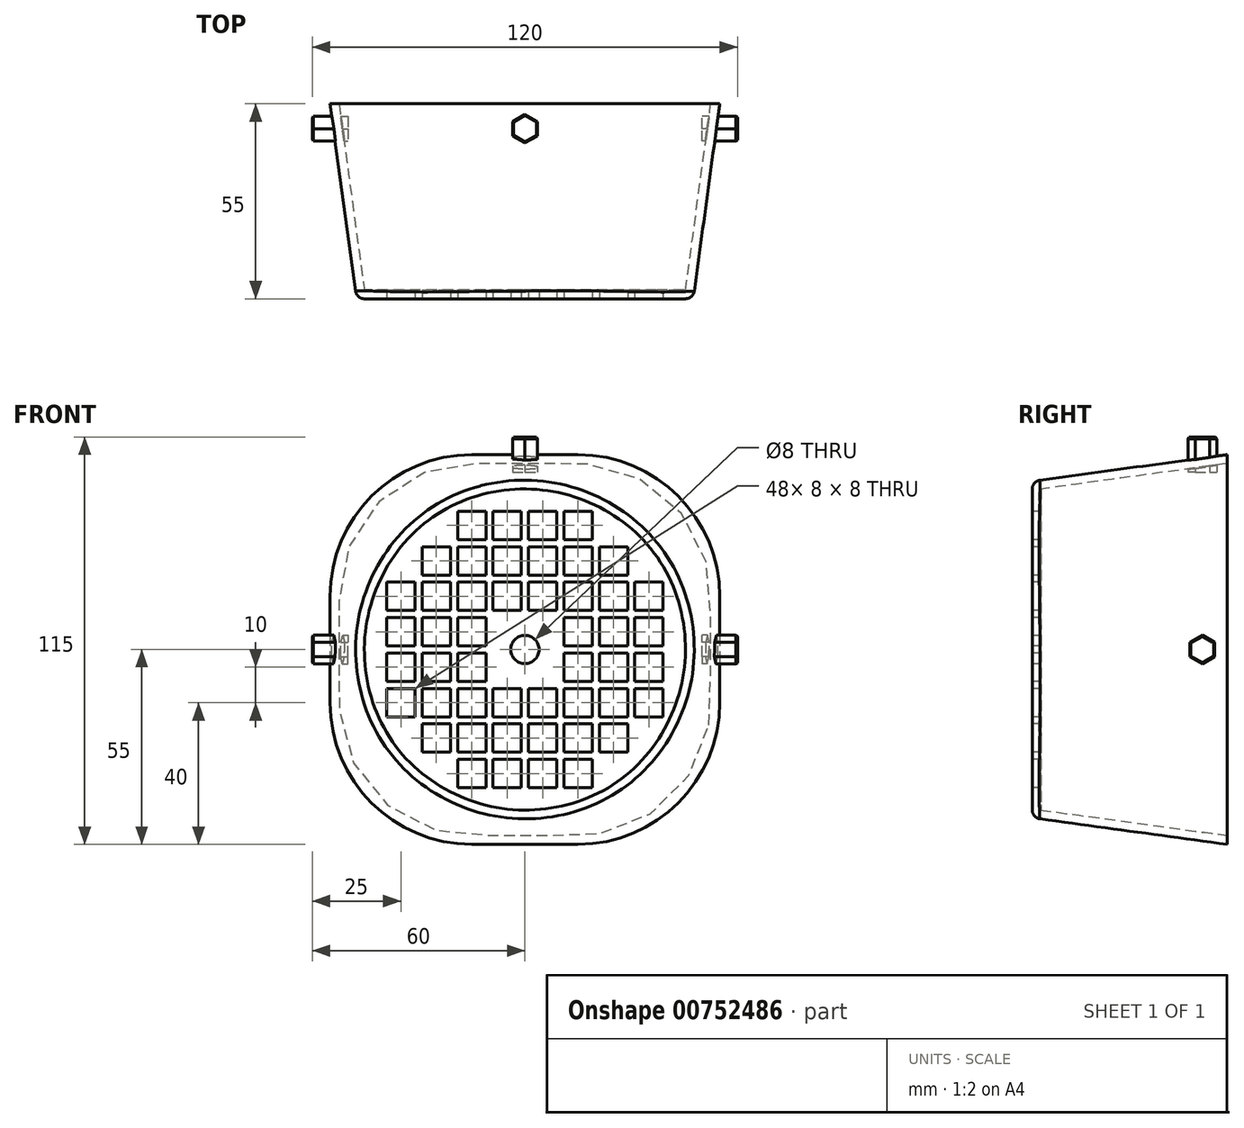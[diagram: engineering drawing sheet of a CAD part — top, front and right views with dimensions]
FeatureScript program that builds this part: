
annotation { "Feature Type Name" : "Feature", "Feature Type Description" : "" }
export const myFeature = defineFeature(function(context is Context, id is Id, definition is map)
    precondition{}
    {
        {
            var Q0;
            Q0=qCreatedBy(makeId("Front.planeOp"),FACE);
            var sketch = newSketch(context, id + "F0", { "sketchPlane" : qUnion([Q0])});
            skLineSegment(sketch, "E0.bottom", {"start": v(-15, 55) * mm, "end": v(15, 55) * mm});
            skLineSegment(sketch, "E0.top", {"start": v(-15, -55) * mm, "end": v(15, -55) * mm});
            skLineSegment(sketch, "E0.left", {"start": v(-55, 15) * mm, "end": v(-55, -15) * mm});
            skLineSegment(sketch, "E0.right", {"start": v(55, 15) * mm, "end": v(55, -15) * mm});
            skPoint(sketch, "E0.middle", {"position": v(0, 0) * mm});
            skPoint(sketch, "E1.visualSharp", {"position": v(-55, 55) * mm});
            skArc(sketch, "E1.filletArc", {"start": v(-15, 55) * mm, "mid": v(-43.28, 43.28) * mm, "end": v(-55, 15) * mm});
            skPoint(sketch, "E2.visualSharp", {"position": v(55, 55) * mm});
            skArc(sketch, "E2.filletArc", {"start": v(55, 15) * mm, "mid": v(43.28, 43.28) * mm, "end": v(15, 55) * mm});
            skPoint(sketch, "E3.visualSharp", {"position": v(55, -55) * mm});
            skArc(sketch, "E3.filletArc", {"start": v(15, -55) * mm, "mid": v(43.28, -43.28) * mm, "end": v(55, -15) * mm});
            skPoint(sketch, "E4.visualSharp", {"position": v(-55, -55) * mm});
            skArc(sketch, "E4.filletArc", {"start": v(-55, -15) * mm, "mid": v(-43.28, -43.28) * mm, "end": v(-15, -55) * mm});
            skSolve(sketch);
        }
        {
            var Q0;
            Q0=qCreatedBy(makeId("Front.planeOp"),FACE);
            cPlane(context, id + "F1", {"entities" : qUnion([Q0]), "cplaneType" : CPlaneType.OFFSET, "offset" : 55 * mm, "width" : 150 * mm, "height" : 150 * mm});
        }
        {
            var Q0;
            Q0=qCreatedBy(id+"F1.planeOp",FACE);
            var sketch = newSketch(context, id + "F2", { "sketchPlane" : qUnion([Q0])});
            skCircle(sketch, "E5", {"center": v(0, 0) * mm, "radius": 47.5 * mm});
            skSolve(sketch);
        }
        {
            var Q0;
            Q0=makeQuery(id+"F0.imprint","IMPRINT",FACE,{"disambiguationData":[TD([[makeQuery(id+"F0.imprint","IMPRINT",EDGE,{"derivedFrom":sQuery(id+"F0.wireOp",EDGE,"E0.bottom")}),-1.0]])]});
            var Q1;
            Q1=makeQuery(id+"F2.imprint","IMPRINT",FACE,{"disambiguationData":[TD([[makeQuery(id+"F2.imprint","IMPRINT",EDGE,{"derivedFrom":sQuery(id+"F2.wireOp",EDGE,"E5")}),1.0]])]});
            loft(context, id + "F3", {"sheetProfilesArray" : [{ "sheetProfileEntities" : qUnion([Q0]) }, { "sheetProfileEntities" : qUnion([Q1]) }]});
        }
        {
            var Q0;
            Q0=makeQuery(id+"F3.opLoft","CAP_FACE",FACE,{"disambiguationData":[OSD([makeQuery(id+"F2.imprint","IMPRINT",FACE,{"disambiguationData":[TD([[makeQuery(id+"F2.imprint","IMPRINT",EDGE,{"derivedFrom":sQuery(id+"F2.wireOp",EDGE,"E5")}),1.0]])]})])],"isStart":true});
            fillet(context, id + "F4", {"entities" : qUnion([Q0]), "radius" : 2.5 * mm, "tangentPropagation" : true, "allowEdgeOverflow" : false});
        }
        {
            var Q0;
            Q0=makeQuery(id+"F3.opLoft","CAP_FACE",FACE,{"disambiguationData":[OSD([makeQuery(id+"F0.imprint","IMPRINT",FACE,{"disambiguationData":[TD([[makeQuery(id+"F0.imprint","IMPRINT",EDGE,{"derivedFrom":sQuery(id+"F0.wireOp",EDGE,"E0.bottom")}),-1.0]])]})])],"isStart":true});
            shell(context, id + "F5", {"entities" : qUnion([Q0]), "thickness" : 2.5 * mm});
        }
        {
            var Q0;
            Q0=makeQuery(id+"F3.opLoft","CAP_FACE",FACE,{"disambiguationData":[OSD([makeQuery(id+"F2.imprint","IMPRINT",FACE,{"disambiguationData":[TD([[makeQuery(id+"F2.imprint","IMPRINT",EDGE,{"derivedFrom":sQuery(id+"F2.wireOp",EDGE,"E5")}),1.0]])]})])],"isStart":true});
            var sketch = newSketch(context, id + "F6", { "sketchPlane" : qUnion([Q0])});
            skLineSegment(sketch, "E6.bottom", {"start": v(11, 11) * mm, "end": v(-11, 11) * mm, "construction": true});
            skLineSegment(sketch, "E6.top", {"start": v(11, -11) * mm, "end": v(-11, -11) * mm, "construction": true});
            skLineSegment(sketch, "E6.left", {"start": v(11, 11) * mm, "end": v(11, -11) * mm, "construction": true});
            skLineSegment(sketch, "E6.right", {"start": v(-11, 11) * mm, "end": v(-11, -11) * mm, "construction": true});
            skPoint(sketch, "E6.middle", {"position": v(0, 0) * mm});
            skLineSegment(sketch, "E7.bottom", {"start": v(-11, 9) * mm, "end": v(-19, 9) * mm});
            skLineSegment(sketch, "E7.top", {"start": v(-11, 1) * mm, "end": v(-19, 1) * mm});
            skLineSegment(sketch, "E7.left", {"start": v(-11, 9) * mm, "end": v(-11, 1) * mm});
            skLineSegment(sketch, "E7.right", {"start": v(-19, 9) * mm, "end": v(-19, 1) * mm});
            skPoint(sketch, "E7.middle", {"position": v(-15, 5) * mm});
            skLineSegment(sketch, "E8.0.1.0", {"start": v(-11, -1) * mm, "end": v(-19, -1) * mm});
            skLineSegment(sketch, "E8.0.1.1", {"start": v(-19, -1) * mm, "end": v(-19, -9) * mm});
            skLineSegment(sketch, "E8.0.1.2", {"start": v(-11, -1) * mm, "end": v(-11, -9) * mm});
            skPoint(sketch, "E8.0.1.3", {"position": v(-15, -5) * mm});
            skLineSegment(sketch, "E8.0.1.4", {"start": v(-11, -9) * mm, "end": v(-19, -9) * mm});
            skLineSegment(sketch, "E8.0.2.0", {"start": v(-11, -11) * mm, "end": v(-19, -11) * mm});
            skLineSegment(sketch, "E8.0.2.1", {"start": v(-19, -11) * mm, "end": v(-19, -19) * mm});
            skLineSegment(sketch, "E8.0.2.2", {"start": v(-11, -11) * mm, "end": v(-11, -19) * mm});
            skPoint(sketch, "E8.0.2.3", {"position": v(-15, -15) * mm});
            skLineSegment(sketch, "E8.0.2.4", {"start": v(-11, -19) * mm, "end": v(-19, -19) * mm});
            skLineSegment(sketch, "E8.0.3.0", {"start": v(-11, -21) * mm, "end": v(-19, -21) * mm});
            skLineSegment(sketch, "E8.0.3.1", {"start": v(-19, -21) * mm, "end": v(-19, -29) * mm});
            skLineSegment(sketch, "E8.0.3.2", {"start": v(-11, -21) * mm, "end": v(-11, -29) * mm});
            skPoint(sketch, "E8.0.3.3", {"position": v(-15, -25) * mm});
            skLineSegment(sketch, "E8.0.3.4", {"start": v(-11, -29) * mm, "end": v(-19, -29) * mm});
            skLineSegment(sketch, "E8.0.4.0", {"start": v(-11, -31) * mm, "end": v(-19, -31) * mm});
            skLineSegment(sketch, "E8.0.4.1", {"start": v(-19, -31) * mm, "end": v(-19, -39) * mm});
            skLineSegment(sketch, "E8.0.4.2", {"start": v(-11, -31) * mm, "end": v(-11, -39) * mm});
            skPoint(sketch, "E8.0.4.3", {"position": v(-15, -35) * mm});
            skLineSegment(sketch, "E8.0.4.4", {"start": v(-11, -39) * mm, "end": v(-19, -39) * mm});
            skLineSegment(sketch, "E8.1.0.0", {"start": v(-21, 9) * mm, "end": v(-29, 9) * mm});
            skLineSegment(sketch, "E8.1.0.1", {"start": v(-29, 9) * mm, "end": v(-29, 1) * mm});
            skLineSegment(sketch, "E8.1.0.2", {"start": v(-21, 9) * mm, "end": v(-21, 1) * mm});
            skPoint(sketch, "E8.1.0.3", {"position": v(-25, 5) * mm});
            skLineSegment(sketch, "E8.1.0.4", {"start": v(-21, 1) * mm, "end": v(-29, 1) * mm});
            skLineSegment(sketch, "E8.1.1.0", {"start": v(-21, -1) * mm, "end": v(-29, -1) * mm});
            skLineSegment(sketch, "E8.1.1.1", {"start": v(-29, -1) * mm, "end": v(-29, -9) * mm});
            skLineSegment(sketch, "E8.1.1.2", {"start": v(-21, -1) * mm, "end": v(-21, -9) * mm});
            skPoint(sketch, "E8.1.1.3", {"position": v(-25, -5) * mm});
            skLineSegment(sketch, "E8.1.1.4", {"start": v(-21, -9) * mm, "end": v(-29, -9) * mm});
            skLineSegment(sketch, "E8.1.2.0", {"start": v(-21, -11) * mm, "end": v(-29, -11) * mm});
            skLineSegment(sketch, "E8.1.2.1", {"start": v(-29, -11) * mm, "end": v(-29, -19) * mm});
            skLineSegment(sketch, "E8.1.2.2", {"start": v(-21, -11) * mm, "end": v(-21, -19) * mm});
            skPoint(sketch, "E8.1.2.3", {"position": v(-25, -15) * mm});
            skLineSegment(sketch, "E8.1.2.4", {"start": v(-21, -19) * mm, "end": v(-29, -19) * mm});
            skLineSegment(sketch, "E8.1.3.0", {"start": v(-21, -21) * mm, "end": v(-29, -21) * mm});
            skLineSegment(sketch, "E8.1.3.1", {"start": v(-29, -21) * mm, "end": v(-29, -29) * mm});
            skLineSegment(sketch, "E8.1.3.2", {"start": v(-21, -21) * mm, "end": v(-21, -29) * mm});
            skPoint(sketch, "E8.1.3.3", {"position": v(-25, -25) * mm});
            skLineSegment(sketch, "E8.1.3.4", {"start": v(-21, -29) * mm, "end": v(-29, -29) * mm});
            skLineSegment(sketch, "E8.2.0.0", {"start": v(-31, 9) * mm, "end": v(-39, 9) * mm});
            skLineSegment(sketch, "E8.2.0.1", {"start": v(-39, 9) * mm, "end": v(-39, 1) * mm});
            skLineSegment(sketch, "E8.2.0.2", {"start": v(-31, 9) * mm, "end": v(-31, 1) * mm});
            skPoint(sketch, "E8.2.0.3", {"position": v(-35, 5) * mm});
            skLineSegment(sketch, "E8.2.0.4", {"start": v(-31, 1) * mm, "end": v(-39, 1) * mm});
            skLineSegment(sketch, "E8.2.1.0", {"start": v(-31, -1) * mm, "end": v(-39, -1) * mm});
            skLineSegment(sketch, "E8.2.1.1", {"start": v(-39, -1) * mm, "end": v(-39, -9) * mm});
            skLineSegment(sketch, "E8.2.1.2", {"start": v(-31, -1) * mm, "end": v(-31, -9) * mm});
            skPoint(sketch, "E8.2.1.3", {"position": v(-35, -5) * mm});
            skLineSegment(sketch, "E8.2.1.4", {"start": v(-31, -9) * mm, "end": v(-39, -9) * mm});
            skLineSegment(sketch, "E8.2.2.0", {"start": v(-31, -11) * mm, "end": v(-39, -11) * mm});
            skLineSegment(sketch, "E8.2.2.1", {"start": v(-39, -11) * mm, "end": v(-39, -19) * mm});
            skLineSegment(sketch, "E8.2.2.2", {"start": v(-31, -11) * mm, "end": v(-31, -19) * mm});
            skPoint(sketch, "E8.2.2.3", {"position": v(-35, -15) * mm});
            skLineSegment(sketch, "E8.2.2.4", {"start": v(-31, -19) * mm, "end": v(-39, -19) * mm});
            skLineSegment(sketch, "E8.direction1", {"start": v(-19, 9) * mm, "end": v(-29, 9) * mm, "construction": true});
            skLineSegment(sketch, "E8.direction2", {"start": v(-19, 9) * mm, "end": v(-19, -1) * mm, "construction": true});
            skLineSegment(sketch, "E9.0.1.0", {"start": v(-11, 19) * mm, "end": v(-19, 19) * mm});
            skLineSegment(sketch, "E9.0.1.1", {"start": v(-11, 19) * mm, "end": v(-11, 11) * mm});
            skLineSegment(sketch, "E9.0.1.2", {"start": v(-19, 19) * mm, "end": v(-19, 11) * mm});
            skLineSegment(sketch, "E9.0.1.3", {"start": v(-11, 11) * mm, "end": v(-19, 11) * mm});
            skLineSegment(sketch, "E9.0.2.0", {"start": v(-11, 29) * mm, "end": v(-19, 29) * mm});
            skLineSegment(sketch, "E9.0.2.1", {"start": v(-11, 29) * mm, "end": v(-11, 21) * mm});
            skLineSegment(sketch, "E9.0.2.2", {"start": v(-19, 29) * mm, "end": v(-19, 21) * mm});
            skLineSegment(sketch, "E9.0.2.3", {"start": v(-11, 21) * mm, "end": v(-19, 21) * mm});
            skLineSegment(sketch, "E9.0.3.0", {"start": v(-11, 39) * mm, "end": v(-19, 39) * mm});
            skLineSegment(sketch, "E9.0.3.1", {"start": v(-11, 39) * mm, "end": v(-11, 31) * mm});
            skLineSegment(sketch, "E9.0.3.2", {"start": v(-19, 39) * mm, "end": v(-19, 31) * mm});
            skLineSegment(sketch, "E9.0.3.3", {"start": v(-11, 31) * mm, "end": v(-19, 31) * mm});
            skLineSegment(sketch, "E9.1.1.0", {"start": v(-1, 19) * mm, "end": v(-9, 19) * mm});
            skLineSegment(sketch, "E9.1.1.1", {"start": v(-1, 19) * mm, "end": v(-1, 11) * mm});
            skLineSegment(sketch, "E9.1.1.2", {"start": v(-9, 19) * mm, "end": v(-9, 11) * mm});
            skLineSegment(sketch, "E9.1.1.3", {"start": v(-1, 11) * mm, "end": v(-9, 11) * mm});
            skLineSegment(sketch, "E9.1.2.0", {"start": v(-1, 29) * mm, "end": v(-9, 29) * mm});
            skLineSegment(sketch, "E9.1.2.1", {"start": v(-1, 29) * mm, "end": v(-1, 21) * mm});
            skLineSegment(sketch, "E9.1.2.2", {"start": v(-9, 29) * mm, "end": v(-9, 21) * mm});
            skLineSegment(sketch, "E9.1.2.3", {"start": v(-1, 21) * mm, "end": v(-9, 21) * mm});
            skLineSegment(sketch, "E9.1.3.0", {"start": v(-1, 39) * mm, "end": v(-9, 39) * mm});
            skLineSegment(sketch, "E9.1.3.1", {"start": v(-1, 39) * mm, "end": v(-1, 31) * mm});
            skLineSegment(sketch, "E9.1.3.2", {"start": v(-9, 39) * mm, "end": v(-9, 31) * mm});
            skLineSegment(sketch, "E9.1.3.3", {"start": v(-1, 31) * mm, "end": v(-9, 31) * mm});
            skLineSegment(sketch, "E9.2.1.0", {"start": v(9, 19) * mm, "end": v(1, 19) * mm});
            skLineSegment(sketch, "E9.2.1.1", {"start": v(9, 19) * mm, "end": v(9, 11) * mm});
            skLineSegment(sketch, "E9.2.1.2", {"start": v(1, 19) * mm, "end": v(1, 11) * mm});
            skLineSegment(sketch, "E9.2.1.3", {"start": v(9, 11) * mm, "end": v(1, 11) * mm});
            skLineSegment(sketch, "E9.2.2.0", {"start": v(9, 29) * mm, "end": v(1, 29) * mm});
            skLineSegment(sketch, "E9.2.2.1", {"start": v(9, 29) * mm, "end": v(9, 21) * mm});
            skLineSegment(sketch, "E9.2.2.2", {"start": v(1, 29) * mm, "end": v(1, 21) * mm});
            skLineSegment(sketch, "E9.2.2.3", {"start": v(9, 21) * mm, "end": v(1, 21) * mm});
            skLineSegment(sketch, "E9.2.3.0", {"start": v(9, 39) * mm, "end": v(1, 39) * mm});
            skLineSegment(sketch, "E9.2.3.1", {"start": v(9, 39) * mm, "end": v(9, 31) * mm});
            skLineSegment(sketch, "E9.2.3.2", {"start": v(1, 39) * mm, "end": v(1, 31) * mm});
            skLineSegment(sketch, "E9.2.3.3", {"start": v(9, 31) * mm, "end": v(1, 31) * mm});
            skLineSegment(sketch, "E9.3.0.0", {"start": v(19, 9) * mm, "end": v(11, 9) * mm});
            skLineSegment(sketch, "E9.3.0.1", {"start": v(19, 9) * mm, "end": v(19, 1) * mm});
            skLineSegment(sketch, "E9.3.0.2", {"start": v(11, 9) * mm, "end": v(11, 1) * mm});
            skLineSegment(sketch, "E9.3.0.3", {"start": v(19, 1) * mm, "end": v(11, 1) * mm});
            skLineSegment(sketch, "E9.3.1.0", {"start": v(19, 19) * mm, "end": v(11, 19) * mm});
            skLineSegment(sketch, "E9.3.1.1", {"start": v(19, 19) * mm, "end": v(19, 11) * mm});
            skLineSegment(sketch, "E9.3.1.2", {"start": v(11, 19) * mm, "end": v(11, 11) * mm});
            skLineSegment(sketch, "E9.3.1.3", {"start": v(19, 11) * mm, "end": v(11, 11) * mm});
            skLineSegment(sketch, "E9.3.2.0", {"start": v(19, 29) * mm, "end": v(11, 29) * mm});
            skLineSegment(sketch, "E9.3.2.1", {"start": v(19, 29) * mm, "end": v(19, 21) * mm});
            skLineSegment(sketch, "E9.3.2.2", {"start": v(11, 29) * mm, "end": v(11, 21) * mm});
            skLineSegment(sketch, "E9.3.2.3", {"start": v(19, 21) * mm, "end": v(11, 21) * mm});
            skLineSegment(sketch, "E9.3.3.0", {"start": v(19, 39) * mm, "end": v(11, 39) * mm});
            skLineSegment(sketch, "E9.3.3.1", {"start": v(19, 39) * mm, "end": v(19, 31) * mm});
            skLineSegment(sketch, "E9.3.3.2", {"start": v(11, 39) * mm, "end": v(11, 31) * mm});
            skLineSegment(sketch, "E9.3.3.3", {"start": v(19, 31) * mm, "end": v(11, 31) * mm});
            skLineSegment(sketch, "E9.4.0.0", {"start": v(29, 9) * mm, "end": v(21, 9) * mm});
            skLineSegment(sketch, "E9.4.0.1", {"start": v(29, 9) * mm, "end": v(29, 1) * mm});
            skLineSegment(sketch, "E9.4.0.2", {"start": v(21, 9) * mm, "end": v(21, 1) * mm});
            skLineSegment(sketch, "E9.4.0.3", {"start": v(29, 1) * mm, "end": v(21, 1) * mm});
            skLineSegment(sketch, "E9.4.1.0", {"start": v(29, 19) * mm, "end": v(21, 19) * mm});
            skLineSegment(sketch, "E9.4.1.1", {"start": v(29, 19) * mm, "end": v(29, 11) * mm});
            skLineSegment(sketch, "E9.4.1.2", {"start": v(21, 19) * mm, "end": v(21, 11) * mm});
            skLineSegment(sketch, "E9.4.1.3", {"start": v(29, 11) * mm, "end": v(21, 11) * mm});
            skLineSegment(sketch, "E9.4.2.0", {"start": v(29, 29) * mm, "end": v(21, 29) * mm});
            skLineSegment(sketch, "E9.4.2.1", {"start": v(29, 29) * mm, "end": v(29, 21) * mm});
            skLineSegment(sketch, "E9.4.2.2", {"start": v(21, 29) * mm, "end": v(21, 21) * mm});
            skLineSegment(sketch, "E9.4.2.3", {"start": v(29, 21) * mm, "end": v(21, 21) * mm});
            skLineSegment(sketch, "E9.direction1", {"start": v(-19, 1) * mm, "end": v(-9, 1) * mm, "construction": true});
            skLineSegment(sketch, "E9.direction2", {"start": v(-19, 1) * mm, "end": v(-19, 11) * mm, "construction": true});
            skLineSegment(sketch, "E10.1.0.4", {"start": v(-21, 29) * mm, "end": v(-29, 29) * mm});
            skLineSegment(sketch, "E10.1.0.5", {"start": v(-21, 29) * mm, "end": v(-21, 21) * mm});
            skLineSegment(sketch, "E10.1.0.6", {"start": v(-21, 21) * mm, "end": v(-29, 21) * mm});
            skLineSegment(sketch, "E10.1.0.7", {"start": v(-21, 19) * mm, "end": v(-29, 19) * mm});
            skLineSegment(sketch, "E10.1.0.8", {"start": v(-21, 19) * mm, "end": v(-21, 11) * mm});
            skLineSegment(sketch, "E10.1.0.9", {"start": v(-21, 11) * mm, "end": v(-29, 11) * mm});
            skLineSegment(sketch, "E10.1.0.10", {"start": v(-29, 19) * mm, "end": v(-29, 11) * mm});
            skLineSegment(sketch, "E10.1.0.11", {"start": v(-29, 29) * mm, "end": v(-29, 21) * mm});
            skLineSegment(sketch, "E10.2.0.7", {"start": v(-31, 19) * mm, "end": v(-39, 19) * mm});
            skLineSegment(sketch, "E10.2.0.8", {"start": v(-31, 19) * mm, "end": v(-31, 11) * mm});
            skLineSegment(sketch, "E10.2.0.9", {"start": v(-31, 11) * mm, "end": v(-39, 11) * mm});
            skLineSegment(sketch, "E10.2.0.10", {"start": v(-39, 19) * mm, "end": v(-39, 11) * mm});
            skLineSegment(sketch, "E10.direction1", {"start": v(-19, 11) * mm, "end": v(-29, 11) * mm, "construction": true});
            skLineSegment(sketch, "E11.0.5.0", {"start": v(39, 9) * mm, "end": v(31, 9) * mm});
            skLineSegment(sketch, "E11.3.5.0", {"start": v(39, 9) * mm, "end": v(39, 1) * mm});
            skLineSegment(sketch, "E11.6.5.0", {"start": v(31, 9) * mm, "end": v(31, 1) * mm});
            skLineSegment(sketch, "E11.9.5.0", {"start": v(39, 1) * mm, "end": v(31, 1) * mm});
            skLineSegment(sketch, "E11.0.5.1", {"start": v(39, 19) * mm, "end": v(31, 19) * mm});
            skLineSegment(sketch, "E11.3.5.1", {"start": v(39, 19) * mm, "end": v(39, 11) * mm});
            skLineSegment(sketch, "E11.6.5.1", {"start": v(31, 19) * mm, "end": v(31, 11) * mm});
            skLineSegment(sketch, "E11.9.5.1", {"start": v(39, 11) * mm, "end": v(31, 11) * mm});
            skLineSegment(sketch, "E12.0.1.1", {"start": v(-9, -1) * mm, "end": v(-9, -9) * mm});
            skLineSegment(sketch, "E12.0.1.6", {"start": v(19, -9) * mm, "end": v(11, -9) * mm});
            skLineSegment(sketch, "E12.0.1.9", {"start": v(19, -1) * mm, "end": v(11, -1) * mm});
            skLineSegment(sketch, "E12.0.1.10", {"start": v(11, -1) * mm, "end": v(11, -9) * mm});
            skLineSegment(sketch, "E12.0.1.11", {"start": v(19, -1) * mm, "end": v(19, -9) * mm});
            skLineSegment(sketch, "E12.0.1.12", {"start": v(21, -1) * mm, "end": v(21, -9) * mm});
            skLineSegment(sketch, "E12.0.1.13", {"start": v(29, -1) * mm, "end": v(29, -9) * mm});
            skLineSegment(sketch, "E12.0.1.14", {"start": v(29, -1) * mm, "end": v(21, -1) * mm});
            skLineSegment(sketch, "E12.0.1.15", {"start": v(29, -9) * mm, "end": v(21, -9) * mm});
            skLineSegment(sketch, "E12.0.1.16", {"start": v(39, -9) * mm, "end": v(31, -9) * mm});
            skLineSegment(sketch, "E12.0.1.17", {"start": v(39, -1) * mm, "end": v(39, -9) * mm});
            skLineSegment(sketch, "E12.0.1.18", {"start": v(39, -1) * mm, "end": v(31, -1) * mm});
            skLineSegment(sketch, "E12.0.1.19", {"start": v(31, -1) * mm, "end": v(31, -9) * mm});
            skLineSegment(sketch, "E12.0.2.0", {"start": v(-1, -19) * mm, "end": v(-9, -19) * mm});
            skLineSegment(sketch, "E12.0.2.1", {"start": v(-9, -11) * mm, "end": v(-9, -19) * mm});
            skLineSegment(sketch, "E12.0.2.2", {"start": v(-1, -11) * mm, "end": v(-9, -11) * mm});
            skLineSegment(sketch, "E12.0.2.3", {"start": v(-1, -11) * mm, "end": v(-1, -19) * mm});
            skLineSegment(sketch, "E12.0.2.4", {"start": v(1, -11) * mm, "end": v(1, -19) * mm});
            skLineSegment(sketch, "E12.0.2.5", {"start": v(9, -11) * mm, "end": v(1, -11) * mm});
            skLineSegment(sketch, "E12.0.2.6", {"start": v(19, -19) * mm, "end": v(11, -19) * mm});
            skLineSegment(sketch, "E12.0.2.7", {"start": v(9, -11) * mm, "end": v(9, -19) * mm});
            skLineSegment(sketch, "E12.0.2.8", {"start": v(9, -19) * mm, "end": v(1, -19) * mm});
            skLineSegment(sketch, "E12.0.2.9", {"start": v(19, -11) * mm, "end": v(11, -11) * mm});
            skLineSegment(sketch, "E12.0.2.10", {"start": v(11, -11) * mm, "end": v(11, -19) * mm});
            skLineSegment(sketch, "E12.0.2.11", {"start": v(19, -11) * mm, "end": v(19, -19) * mm});
            skLineSegment(sketch, "E12.0.2.12", {"start": v(21, -11) * mm, "end": v(21, -19) * mm});
            skLineSegment(sketch, "E12.0.2.13", {"start": v(29, -11) * mm, "end": v(29, -19) * mm});
            skLineSegment(sketch, "E12.0.2.14", {"start": v(29, -11) * mm, "end": v(21, -11) * mm});
            skLineSegment(sketch, "E12.0.2.15", {"start": v(29, -19) * mm, "end": v(21, -19) * mm});
            skLineSegment(sketch, "E12.0.2.16", {"start": v(39, -19) * mm, "end": v(31, -19) * mm});
            skLineSegment(sketch, "E12.0.2.17", {"start": v(39, -11) * mm, "end": v(39, -19) * mm});
            skLineSegment(sketch, "E12.0.2.18", {"start": v(39, -11) * mm, "end": v(31, -11) * mm});
            skLineSegment(sketch, "E12.0.2.19", {"start": v(31, -11) * mm, "end": v(31, -19) * mm});
            skLineSegment(sketch, "E12.0.3.0", {"start": v(-1, -29) * mm, "end": v(-9, -29) * mm});
            skLineSegment(sketch, "E12.0.3.1", {"start": v(-9, -21) * mm, "end": v(-9, -29) * mm});
            skLineSegment(sketch, "E12.0.3.2", {"start": v(-1, -21) * mm, "end": v(-9, -21) * mm});
            skLineSegment(sketch, "E12.0.3.3", {"start": v(-1, -21) * mm, "end": v(-1, -29) * mm});
            skLineSegment(sketch, "E12.0.3.4", {"start": v(1, -21) * mm, "end": v(1, -29) * mm});
            skLineSegment(sketch, "E12.0.3.5", {"start": v(9, -21) * mm, "end": v(1, -21) * mm});
            skLineSegment(sketch, "E12.0.3.6", {"start": v(19, -29) * mm, "end": v(11, -29) * mm});
            skLineSegment(sketch, "E12.0.3.7", {"start": v(9, -21) * mm, "end": v(9, -29) * mm});
            skLineSegment(sketch, "E12.0.3.8", {"start": v(9, -29) * mm, "end": v(1, -29) * mm});
            skLineSegment(sketch, "E12.0.3.9", {"start": v(19, -21) * mm, "end": v(11, -21) * mm});
            skLineSegment(sketch, "E12.0.3.10", {"start": v(11, -21) * mm, "end": v(11, -29) * mm});
            skLineSegment(sketch, "E12.0.3.11", {"start": v(19, -21) * mm, "end": v(19, -29) * mm});
            skLineSegment(sketch, "E12.0.3.12", {"start": v(21, -21) * mm, "end": v(21, -29) * mm});
            skLineSegment(sketch, "E12.0.3.13", {"start": v(29, -21) * mm, "end": v(29, -29) * mm});
            skLineSegment(sketch, "E12.0.3.14", {"start": v(29, -21) * mm, "end": v(21, -21) * mm});
            skLineSegment(sketch, "E12.0.3.15", {"start": v(29, -29) * mm, "end": v(21, -29) * mm});
            skLineSegment(sketch, "E12.0.4.0", {"start": v(-1, -39) * mm, "end": v(-9, -39) * mm});
            skLineSegment(sketch, "E12.0.4.1", {"start": v(-9, -31) * mm, "end": v(-9, -39) * mm});
            skLineSegment(sketch, "E12.0.4.2", {"start": v(-1, -31) * mm, "end": v(-9, -31) * mm});
            skLineSegment(sketch, "E12.0.4.3", {"start": v(-1, -31) * mm, "end": v(-1, -39) * mm});
            skLineSegment(sketch, "E12.0.4.4", {"start": v(1, -31) * mm, "end": v(1, -39) * mm});
            skLineSegment(sketch, "E12.0.4.5", {"start": v(9, -31) * mm, "end": v(1, -31) * mm});
            skLineSegment(sketch, "E12.0.4.6", {"start": v(19, -39) * mm, "end": v(11, -39) * mm});
            skLineSegment(sketch, "E12.0.4.7", {"start": v(9, -31) * mm, "end": v(9, -39) * mm});
            skLineSegment(sketch, "E12.0.4.8", {"start": v(9, -39) * mm, "end": v(1, -39) * mm});
            skLineSegment(sketch, "E12.0.4.9", {"start": v(19, -31) * mm, "end": v(11, -31) * mm});
            skLineSegment(sketch, "E12.0.4.10", {"start": v(11, -31) * mm, "end": v(11, -39) * mm});
            skLineSegment(sketch, "E12.0.4.11", {"start": v(19, -31) * mm, "end": v(19, -39) * mm});
            skLineSegment(sketch, "E12.direction1", {"start": v(-9, 1) * mm, "end": v(57.2, 1) * mm, "construction": true});
            skCircle(sketch, "E13", {"center": v(0, 0) * mm, "radius": 4 * mm});
            skSolve(sketch);
        }
        {
            var Q0;
            Q0 = qSketchRegion(id + "F6", true);
            extrude(context, id + "F7", {"entities" : qUnion([Q0]), "operationType" : NewBodyOperationType.REMOVE, "endBound" : BoundingType.UP_TO_NEXT, "oppositeDirection" : true, "depth" : 25 * mm, "offsetDistance" : 25 * mm});
        }
        {
            var Q0;
            Q0=makeQuery(id+"F3.opLoft","CAP_FACE",FACE,{"disambiguationData":[OSD([makeQuery(id+"F0.imprint","IMPRINT",FACE,{"disambiguationData":[TD([[makeQuery(id+"F0.imprint","IMPRINT",EDGE,{"derivedFrom":sQuery(id+"F0.wireOp",EDGE,"E0.bottom")}),-1.0]])]})])],"isStart":true});
            var sketch = newSketch(context, id + "F8", { "sketchPlane" : qUnion([Q0])});
            skCircle(sketch, "E14", {"center": v(0, 0) * mm, "radius": 45 * mm});
            skSolve(sketch);
        }
        {
            var Q0;
            Q0=qCreatedBy(makeId("Right.planeOp"),FACE);
            cPlane(context, id + "F9", {"entities" : qUnion([Q0]), "cplaneType" : CPlaneType.OFFSET, "offset" : 55 * mm, "width" : 150 * mm, "height" : 150 * mm});
        }
        {
            var Q0;
            Q0=qCreatedBy(makeId("Right.planeOp"),FACE);
            cPlane(context, id + "F10", {"entities" : qUnion([Q0]), "cplaneType" : CPlaneType.OFFSET, "offset" : 55 * mm, "oppositeDirection" : true, "width" : 150 * mm, "height" : 150 * mm});
        }
        {
            var Q0;
            Q0=qCreatedBy(id+"F10.planeOp",FACE);
            var sketch = newSketch(context, id + "F11", { "sketchPlane" : qUnion([Q0])});
            skCircle(sketch, "E15.cCircle", {"center": v(-7, 0) * mm, "radius": 3.5 * mm, "construction": true});
            skLineSegment(sketch, "E15.0", {"start": v(-10.5, -2.02) * mm, "end": v(-10.5, 2.02) * mm});
            skLineSegment(sketch, "E15.1", {"start": v(-10.5, 2.02) * mm, "end": v(-7, 4.04) * mm});
            skLineSegment(sketch, "E15.2", {"start": v(-7, 4.04) * mm, "end": v(-3.5, 2.02) * mm});
            skLineSegment(sketch, "E15.3", {"start": v(-3.5, 2.02) * mm, "end": v(-3.5, -2.02) * mm});
            skLineSegment(sketch, "E15.4", {"start": v(-3.5, -2.02) * mm, "end": v(-7, -4.04) * mm});
            skLineSegment(sketch, "E15.5", {"start": v(-7, -4.04) * mm, "end": v(-10.5, -2.02) * mm});
            skPoint(sketch, "E15.0.midPoint", {"position": v(-10.5, 0) * mm});
            skLineSegment(sketch, "E16", {"start": v(-7, 0) * mm, "end": v(0, 0) * mm, "construction": true});
            skSolve(sketch);
        }
        {
            var Q0;
            Q0 = qSketchRegion(id + "F11", true);
            var Q1;
            Q1=makeQuery(id+"F3.opLoft","SWEPT_FACE",FACE,{"disambiguationData":[OSD([sQuery(id+"F0.wireOp",EDGE,"E0.bottom"),sQuery(id+"F0.wireOp",EDGE,"E0.left"),sQuery(id+"F0.wireOp",EDGE,"E1.filletArc"),sQuery(id+"F2.wireOp",EDGE,"E5")])]});
            extrude(context, id + "F12", {"entities" : qUnion([Q0]), "operationType" : NewBodyOperationType.ADD, "oppositeDirection" : true, "depth" : 5 * mm, "offsetDistance" : 25 * mm, "hasSecondDirection" : true, "secondDirectionOppositeDirection" : false, "secondDirectionDepth" : 5 * mm, "secondDirectionBoundEntityFace" : qUnion([Q1])});
        }
        {
            var Q0;
            Q0=qCreatedBy(id+"F9.planeOp",FACE);
            var sketch = newSketch(context, id + "F13", { "sketchPlane" : qUnion([Q0])});
            skCircle(sketch, "E17.cCircle", {"center": v(-7, 0) * mm, "radius": 3.5 * mm, "construction": true});
            skLineSegment(sketch, "E17.0", {"start": v(-10.5, -2.02) * mm, "end": v(-10.5, 2.02) * mm});
            skLineSegment(sketch, "E17.1", {"start": v(-10.5, 2.02) * mm, "end": v(-7, 4.04) * mm});
            skLineSegment(sketch, "E17.2", {"start": v(-7, 4.04) * mm, "end": v(-3.5, 2.02) * mm});
            skLineSegment(sketch, "E17.3", {"start": v(-3.5, 2.02) * mm, "end": v(-3.5, -2.02) * mm});
            skLineSegment(sketch, "E17.4", {"start": v(-3.5, -2.02) * mm, "end": v(-7, -4.04) * mm});
            skLineSegment(sketch, "E17.5", {"start": v(-7, -4.04) * mm, "end": v(-10.5, -2.02) * mm});
            skPoint(sketch, "E17.0.midPoint", {"position": v(-10.5, 0) * mm});
            skLineSegment(sketch, "E18", {"start": v(-7, 0) * mm, "end": v(0, 0) * mm, "construction": true});
            skSolve(sketch);
        }
        {
            var Q0;
            Q0 = qSketchRegion(id + "F13", true);
            extrude(context, id + "F14", {"entities" : qUnion([Q0]), "operationType" : NewBodyOperationType.ADD, "depth" : 5 * mm, "offsetDistance" : 25 * mm, "hasSecondDirection" : true, "secondDirectionOppositeDirection" : true, "secondDirectionDepth" : 5 * mm});
        }
        {
            var Q0;
            Q0=qCreatedBy(makeId("Top.planeOp"),FACE);
            cPlane(context, id + "F15", {"entities" : qUnion([Q0]), "cplaneType" : CPlaneType.OFFSET, "offset" : 55 * mm, "width" : 150 * mm, "height" : 150 * mm});
        }
        {
            var Q0;
            Q0=qCreatedBy(id+"F15.planeOp",FACE);
            var sketch = newSketch(context, id + "F16", { "sketchPlane" : qUnion([Q0])});
            skCircle(sketch, "E19.cCircle", {"center": v(0, -7) * mm, "radius": 3.5 * mm, "construction": true});
            skLineSegment(sketch, "E19.0", {"start": v(-3.5, -9.02) * mm, "end": v(-3.5, -4.98) * mm});
            skLineSegment(sketch, "E19.1", {"start": v(-3.5, -4.98) * mm, "end": v(0, -2.96) * mm});
            skLineSegment(sketch, "E19.2", {"start": v(0, -2.96) * mm, "end": v(3.5, -4.98) * mm});
            skLineSegment(sketch, "E19.3", {"start": v(3.5, -4.98) * mm, "end": v(3.5, -9.02) * mm});
            skLineSegment(sketch, "E19.4", {"start": v(3.5, -9.02) * mm, "end": v(0, -11.04) * mm});
            skLineSegment(sketch, "E19.5", {"start": v(0, -11.04) * mm, "end": v(-3.5, -9.02) * mm});
            skPoint(sketch, "E19.0.midPoint", {"position": v(-3.5, -7) * mm});
            skLineSegment(sketch, "E20", {"start": v(0, -7) * mm, "end": v(0, 0) * mm, "construction": true});
            skSolve(sketch);
        }
        {
            var Q0;
            Q0 = qSketchRegion(id + "F16", true);
            extrude(context, id + "F17", {"entities" : qUnion([Q0]), "operationType" : NewBodyOperationType.ADD, "depth" : 5 * mm, "offsetDistance" : 25 * mm, "hasSecondDirection" : true, "secondDirectionOppositeDirection" : true, "secondDirectionDepth" : 5 * mm});
        }
        {
            var Q0;
            Q0=makeQuery(id+"F12.opExtrude","CAP_EDGE",EDGE,{"disambiguationData":[OSD([sQuery(id+"F11.wireOp",EDGE,"E15.3")])],"isStart":false});
            var Q1;
            Q1=makeQuery(id+"F12.opExtrude","CAP_EDGE",EDGE,{"disambiguationData":[OSD([sQuery(id+"F11.wireOp",EDGE,"E15.4")])],"isStart":false});
            var Q2;
            Q2=makeQuery(id+"F12.opExtrude","CAP_EDGE",EDGE,{"disambiguationData":[OSD([sQuery(id+"F11.wireOp",EDGE,"E15.5")])],"isStart":false});
            var Q3;
            Q3=makeQuery(id+"F12.opExtrude","CAP_EDGE",EDGE,{"disambiguationData":[OSD([sQuery(id+"F11.wireOp",EDGE,"E15.0")])],"isStart":false});
            var Q4;
            Q4=makeQuery(id+"F12.opExtrude","CAP_EDGE",EDGE,{"disambiguationData":[OSD([sQuery(id+"F11.wireOp",EDGE,"E15.1")])],"isStart":false});
            var Q5;
            Q5=makeQuery(id+"F12.opExtrude","CAP_EDGE",EDGE,{"disambiguationData":[OSD([sQuery(id+"F11.wireOp",EDGE,"E15.2")])],"isStart":false});
            var Q6;
            Q6=makeQuery(id+"F17.opExtrude","CAP_EDGE",EDGE,{"disambiguationData":[OSD([sQuery(id+"F16.wireOp",EDGE,"E19.1")])],"isStart":false});
            var Q7;
            Q7=makeQuery(id+"F17.opExtrude","CAP_EDGE",EDGE,{"disambiguationData":[OSD([sQuery(id+"F16.wireOp",EDGE,"E19.2")])],"isStart":false});
            var Q8;
            Q8=makeQuery(id+"F17.opExtrude","CAP_EDGE",EDGE,{"disambiguationData":[OSD([sQuery(id+"F16.wireOp",EDGE,"E19.3")])],"isStart":false});
            var Q9;
            Q9=makeQuery(id+"F17.opExtrude","CAP_EDGE",EDGE,{"disambiguationData":[OSD([sQuery(id+"F16.wireOp",EDGE,"E19.4")])],"isStart":false});
            var Q10;
            Q10=makeQuery(id+"F17.opExtrude","CAP_EDGE",EDGE,{"disambiguationData":[OSD([sQuery(id+"F16.wireOp",EDGE,"E19.5")])],"isStart":false});
            var Q11;
            Q11=makeQuery(id+"F17.opExtrude","CAP_EDGE",EDGE,{"disambiguationData":[OSD([sQuery(id+"F16.wireOp",EDGE,"E19.0")])],"isStart":false});
            var Q12;
            Q12=makeQuery(id+"F14.opExtrude","CAP_EDGE",EDGE,{"disambiguationData":[OSD([sQuery(id+"F13.wireOp",EDGE,"E17.4")])],"isStart":false});
            var Q13;
            Q13=makeQuery(id+"F14.opExtrude","CAP_EDGE",EDGE,{"disambiguationData":[OSD([sQuery(id+"F13.wireOp",EDGE,"E17.5")])],"isStart":false});
            var Q14;
            Q14=makeQuery(id+"F14.opExtrude","CAP_EDGE",EDGE,{"disambiguationData":[OSD([sQuery(id+"F13.wireOp",EDGE,"E17.3")])],"isStart":false});
            var Q15;
            Q15=makeQuery(id+"F14.opExtrude","CAP_EDGE",EDGE,{"disambiguationData":[OSD([sQuery(id+"F13.wireOp",EDGE,"E17.2")])],"isStart":false});
            var Q16;
            Q16=makeQuery(id+"F14.opExtrude","CAP_EDGE",EDGE,{"disambiguationData":[OSD([sQuery(id+"F13.wireOp",EDGE,"E17.1")])],"isStart":false});
            var Q17;
            Q17=makeQuery(id+"F14.opExtrude","CAP_EDGE",EDGE,{"disambiguationData":[OSD([sQuery(id+"F13.wireOp",EDGE,"E17.0")])],"isStart":false});
            chamfer(context, id + "F18", {"entities" : qUnion([Q0, Q1, Q2, Q3, Q4, Q5, Q6, Q7, Q8, Q9, Q10, Q11, Q12, Q13, Q14, Q15, Q16, Q17]), "chamferType" : ChamferType.TWO_OFFSETS, "width1" : .5 * mm, "oppositeDirection" : false, "width2" : .25 * mm});
        }
    });
